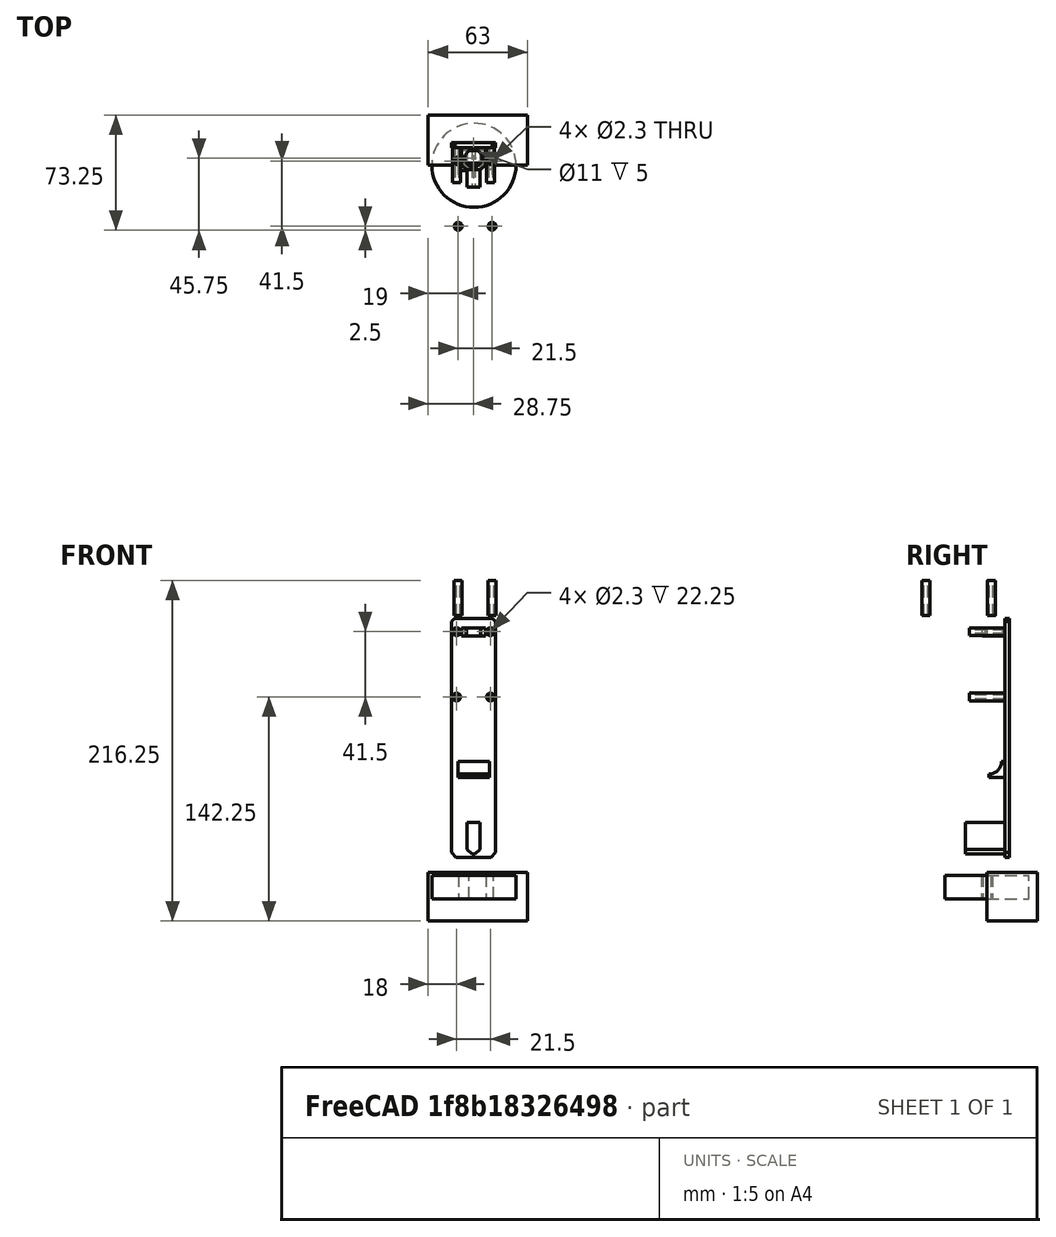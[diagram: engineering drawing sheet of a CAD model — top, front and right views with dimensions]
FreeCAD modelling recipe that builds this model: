
FCSTD DOCUMENT  (FreeCAD 0.19R14555 (Git shallow))
Label: hydrostatus-assembly
License: All rights reserved
LicenseURL: http://en.wikipedia.org/wiki/All_rights_reserved
objects: TechDraw::DrawViewDimension×17, Part::Chamfer×9, Part::Box×6, Part::FeaturePython×6, Part::Cut×3, TechDraw::DrawViewPart×3, Part::Cylinder×2, Sketcher::SketchObject×2, App::LinkGroup×1, PartDesign::ShapeBinder×1, PartDesign::Pad×1, PartDesign::Pocket×1, PartDesign::Body×1, TechDraw::DrawSVGTemplate×1, TechDraw::DrawPage×1
note: 34 computed .brp shape members not serialized (recipe doc carries the construction recipe); baked Part::Feature solids carry a one-line shape summary decoded from their .brp

FEATURE [Part::Box] Box  label="Cube"
  AttacherType = Attacher::AttachEngine3D
  Height = 3
  Length = 28
  Placement = pos=(-13.25,-148.75,-3.25) rot=(0,0,1;0rad)
  Width = 160
FEATURE [Part::Box] Box001  label="Cube001"
  AttacherType = Attacher::AttachEngine3D
  Height = 25
  Length = 8
  Placement = pos=(-3.25,-138.5,0) rot=(0,0,1;0rad)
  Width = 20
FEATURE [Part::Box] Box002  label="Cube002"
  AttacherType = Attacher::AttachEngine3D
  Height = 10
  Length = 20
  Placement = pos=(-9.25,-89.75,-0.25) rot=(0,0,1;0rad)
  Width = 10
FEATURE [Part::Chamfer] Chamfer
  Base = -> Box002
  Edges = 1 edges r=4: [Edge12]
FEATURE [Part::Chamfer] Chamfer001
  Base = -> Box001
  Edges = 1 edges r=3: [Edge5]
FEATURE [Part::Chamfer] Chamfer002
  Base = -> Chamfer001
  Edges = 1 edges r=3: [Edge15]
  Placement = pos=(0,0,-0.25) rot=(0,0,1;0rad)
FEATURE [Part::Cylinder] Cylinder
  Angle = 360
  AttacherType = Attacher::AttachEngine3D
  Height = 64
  Placement = pos=(1,-52.75,6.5) rot=(-1,0,0;1.5708rad)
  Radius = 5.5
FEATURE [Part::Chamfer] Chamfer003
  Base = -> Box
  Edges = 1 edges r=2: [Edge7]
FEATURE [Part::Chamfer] Chamfer004
  Base = -> Chamfer003
  Edges = 1 edges r=2: [Edge15]
FEATURE [Part::Chamfer] Chamfer005
  Base = -> Chamfer004
  Edges = 1 edges r=2: [Edge16]
FEATURE [Part::Chamfer] Chamfer006
  Base = -> Chamfer005
  Edges = 1 edges r=2: [Edge9]
FEATURE [Part::Box] Box003  label="Cube003"
  AttacherType = Attacher::AttachEngine3D
  Height = 14
  Length = 15
  Placement = pos=(-6.5,0,-0.25) rot=(0,0,1;0rad)
  Width = 5
FEATURE [Part::Cut] Cut
  Base = -> Box003
  Tool = -> Cylinder
FEATURE [Part::Chamfer] Chamfer007
  Base = -> Cut
  Edges = 2 edges r=3: [Edge2,Edge10]
  Placement = pos=(-0.25,0,0) rot=(0,0,1;0rad)
FEATURE [Part::FeaturePython] Tube  # WARN: FeaturePython — macro-defined, semantics opaque (R4)
  AttacherType = Attacher::AttachEngine3D
  Height = 22.25
  InnerRadius = 1.15
  OuterRadius = 2.5
  Placement = pos=(-10,-38.75,0) rot=(0,0,1;0rad)
FEATURE [Part::FeaturePython] Tube001  # WARN: FeaturePython — macro-defined, semantics opaque (R4)
  AttacherType = Attacher::AttachEngine3D
  Height = 22.25
  InnerRadius = 1.15
  OuterRadius = 2.5
  Placement = pos=(11.5,-38.75,0) rot=(0,0,1;0rad)
FEATURE [Part::FeaturePython] Tube002  # WARN: FeaturePython — macro-defined, semantics opaque (R4)
  AttacherType = Attacher::AttachEngine3D
  Height = 22.25
  InnerRadius = 1.15
  OuterRadius = 2.5
  Placement = pos=(-10,2.75,0) rot=(0,0,1;0rad)
FEATURE [Part::FeaturePython] Tube003  # WARN: FeaturePython — macro-defined, semantics opaque (R4)
  AttacherType = Attacher::AttachEngine3D
  Height = 22.25
  InnerRadius = 1.15
  OuterRadius = 2.5
  Placement = pos=(11.5,2.75,0) rot=(0,0,1;0rad)
FEATURE [App::LinkGroup] LinkGroup
  ElementList = -> [Tube,Tube001,Tube002,Tube003]
  LinkMode = 0
  Placement = pos=(0,2.38419e-06,-0.250001) rot=(0,0,1;0rad)
FEATURE [Part::Box] Box004  label="Cube004"
  AttacherType = Attacher::AttachEngine3D
  Height = 20
  Length = 38
  Placement = pos=(-18.5,-152.5,-9.75) rot=(0,0,1;0rad)
  Width = 12
FEATURE [Part::Cut] Cut001
  Base = -> Chamfer006
  Tool = -> Box004
FEATURE [Part::Chamfer] Chamfer008
  Base = -> Cut001
  Edges = 2 edges r=3: [Edge9,Edge17]
FEATURE [Part::Cylinder] Cylinder001
  Angle = 360
  AttacherType = Attacher::AttachEngine3D
  Height = 24
  Placement = pos=(12.5,-79.75,9.75) rot=(0,-1,0;1.5708rad)
  Radius = 8
FEATURE [Part::Cut] Cut002
  Base = -> Chamfer
  Tool = -> Cylinder001
FEATURE [Part::FeaturePython] Connect  # WARN: FeaturePython — macro-defined, semantics opaque (R4)
  Objects = -> [Chamfer002,Chamfer007,LinkGroup,Chamfer008,Cut002]
  Placement = pos=(-1,11,-13) rot=(1,0,0;1.5708rad)
  Tolerance = 0
FEATURE [PartDesign::ShapeBinder] CopyPad001
  TraceSupport = false
FEATURE [Sketcher::SketchObject] Sketch002
  FullyConstrained = true
  MapMode = 5
  Placement = pos=(0,0,0) rot=(1,0,0;3.14159rad)
  Support = -> [CopyPad001]
  sketch-geometry (1):
    g0: Circle CenterX=0 CenterY=0 CenterZ=0 NormalX=0 NormalY=0 NormalZ=1 AngleXU=0 Radius=26.72
  constraints (2):
    c: Coincident(g0,g-1)
    c: Diameter(g0) = 53.44
FEATURE [PartDesign::Pad] Pad002
  Direction = (1,1,1)
  Length = 15
  Length2 = 100
  Profile = -> Sketch002
  Type = 0
FEATURE [Sketcher::SketchObject] Sketch003
  FullyConstrained = true
  MapMode = 5
  Placement = pos=(0,0,-15) rot=(1,0,0;3.14159rad)
  Support = -> [Pad002]
  sketch-geometry (2):
    g0: Circle CenterX=-6.45052 CenterY=0 CenterZ=0 NormalX=0 NormalY=0 NormalZ=1 AngleXU=0 Radius=3.475
    g1: Circle CenterX=10.0263 CenterY=0 CenterZ=0 NormalX=0 NormalY=0 NormalZ=1 AngleXU=0 Radius=2.425
  constraints (6):
    c: PointOnObject(g0,g-1)
    c: PointOnObject(g1,g-1)
    c: Diameter(g1) = 4.85
    c: Diameter(g0) = 6.95
    c: DistanceX(g0) = -6.45052
    c: DistanceX(g1) = 10.0263
FEATURE [PartDesign::Pocket] Pocket
  BaseFeature = -> Pad002
  Length = 0
  Length2 = 100
  Profile = -> Sketch003
  Type = 2
FEATURE [PartDesign::Body] Body002  label="pvc_cable_boot"
  Group = -> [CopyPad001,Sketch002,Pad002,Sketch003,Pocket]
  Origin = -> Origin002
  Placement = pos=(0,0,-165) rot=(0,0,1;0rad)
  Tip = -> Pocket
FEATURE [Part::Box] Box005  label="Cube005"
  AttacherType = Attacher::AttachEngine3D
  Height = 31
  Length = 63
  Placement = pos=(-29,0,-194) rot=(0,0,1;0rad)
  Width = 32
FEATURE [Part::FeaturePython] Slice  # WARN: FeaturePython — macro-defined, semantics opaque (R4)
  Base = -> Body002
  Mode = 1
  Tolerance = 0
  Tools = -> [Box005]
FEATURE [TechDraw::DrawSVGTemplate] Template
  Height = 210
  Orientation = 1
  Width = 297
FEATURE [TechDraw::DrawViewPart] View
  Caption = electronics assembly top view
  CoarseView = false
  Direction = (0,-1,0)
  Focus = 100
  HardHidden = false
  IsoCount = 0
  IsoHidden = false
  IsoVisible = false
  LockPosition = false
  Perspective = false
  Rotation = 0
  ScaleType = 0
  SeamHidden = false
  SeamVisible = true
  SmoothHidden = false
  SmoothVisible = true
  Source = -> [Connect]
  X = 149.857
  XDirection = (0,0,-1)
  Y = 53.4468
FEATURE [TechDraw::DrawViewPart] View001
  Caption = electronics assembly 45*d view
  CoarseView = false
  Direction = (-0.707,-0.707,0)
  Focus = 100
  HardHidden = false
  IsoCount = 0
  IsoHidden = false
  IsoVisible = false
  LockPosition = false
  Perspective = false
  Rotation = 0
  ScaleType = 0
  SeamHidden = false
  SeamVisible = true
  SmoothHidden = false
  SmoothVisible = true
  Source = -> [Connect]
  X = 149.857
  XDirection = (0,0,-1)
  Y = 106.017
FEATURE [TechDraw::DrawViewPart] View002
  Caption = electronics assembly side profile
  CoarseView = false
  Direction = (-1,0,0)
  Focus = 100
  HardHidden = false
  IsoCount = 0
  IsoHidden = false
  IsoVisible = false
  LockPosition = false
  Perspective = false
  Rotation = 0
  ScaleType = 0
  SeamHidden = false
  SeamVisible = true
  SmoothHidden = false
  SmoothVisible = true
  Source = -> [Connect]
  X = 149.857
  XDirection = (0,0,-1)
  Y = 158.249
FEATURE [TechDraw::DrawViewDimension] Dimension
  Arbitrary = false
  ArbitraryTolerances = false
  EqualTolerance = true
  FormatSpec = %.2f
  FormatSpecOverTolerance = %+.2f
  FormatSpecUnderTolerance = %+.2f
  Inverted = false
  LockPosition = false
  MeasureType = 1
  OverTolerance = 0
  References2D = -> [View]
  Rotation = 0
  ScaleType = 0
  TheoreticalExact = false
  Type = 2
  UnderTolerance = 0
  X = 79.6211
  Y = -9.54121
FEATURE [TechDraw::DrawViewDimension] Dimension001
  Arbitrary = false
  ArbitraryTolerances = false
  EqualTolerance = true
  FormatSpec = %.2f
  FormatSpecOverTolerance = %+.2f
  FormatSpecUnderTolerance = %+.2f
  Inverted = false
  LockPosition = false
  MeasureType = 1
  OverTolerance = 0
  References2D = -> [View]
  Rotation = 0
  ScaleType = 0
  TheoreticalExact = false
  Type = 1
  UnderTolerance = 0
  X = 39.1592
  Y = 23.0334
FEATURE [TechDraw::DrawViewDimension] Dimension002
  Arbitrary = false
  ArbitraryTolerances = false
  EqualTolerance = true
  FormatSpec = %.2f
  FormatSpecOverTolerance = %+.2f
  FormatSpecUnderTolerance = %+.2f
  Inverted = false
  LockPosition = false
  MeasureType = 1
  OverTolerance = 0
  References2D = -> [View]
  Rotation = 0
  ScaleType = 0
  TheoreticalExact = false
  Type = 2
  UnderTolerance = 0
  X = 10.3544
  Y = 0.227172
FEATURE [TechDraw::DrawViewDimension] Dimension003
  Arbitrary = false
  ArbitraryTolerances = false
  EqualTolerance = true
  FormatSpec = %.2f
  FormatSpecOverTolerance = %+.2f
  FormatSpecUnderTolerance = %+.2f
  Inverted = false
  LockPosition = false
  MeasureType = 1
  OverTolerance = 0
  References2D = -> [View]
  Rotation = 0
  ScaleType = 0
  TheoreticalExact = false
  Type = 1
  UnderTolerance = 0
  X = 62.375
  Y = -6.83965
FEATURE [TechDraw::DrawViewDimension] Dimension005
  Arbitrary = false
  ArbitraryTolerances = false
  EqualTolerance = true
  FormatSpec = %.2f
  FormatSpecOverTolerance = %+.2f
  FormatSpecUnderTolerance = %+.2f
  Inverted = false
  LockPosition = false
  MeasureType = 1
  OverTolerance = 0
  References2D = -> [View002]
  Rotation = 0
  ScaleType = 0
  TheoreticalExact = false
  Type = 2
  UnderTolerance = 0
  X = 78.7503
  Y = 3.43096
FEATURE [TechDraw::DrawViewDimension] Dimension006
  Arbitrary = false
  ArbitraryTolerances = false
  EqualTolerance = true
  FormatSpec = ⌀%.2f
  FormatSpecOverTolerance = %+.2f
  FormatSpecUnderTolerance = %+.2f
  Inverted = false
  LockPosition = false
  MeasureType = 1
  OverTolerance = 0
  References2D = -> [View]
  Rotation = 0
  ScaleType = 0
  TheoreticalExact = false
  Type = 5
  UnderTolerance = 0
  X = -15.8415
  Y = -7.03338
FEATURE [TechDraw::DrawViewDimension] Dimension007
  Arbitrary = false
  ArbitraryTolerances = false
  EqualTolerance = true
  FormatSpec = ⌀%.2f
  FormatSpecOverTolerance = %+.2f
  FormatSpecUnderTolerance = %+.2f
  Inverted = false
  LockPosition = false
  MeasureType = 1
  OverTolerance = 0
  References2D = -> [View]
  Rotation = 0
  ScaleType = 0
  TheoreticalExact = false
  Type = 5
  UnderTolerance = 0
  X = -19.4568
  Y = -0.52586
FEATURE [TechDraw::DrawViewDimension] Dimension008
  Arbitrary = false
  ArbitraryTolerances = false
  EqualTolerance = true
  FormatSpec = %.2f
  FormatSpecOverTolerance = %+.2f
  FormatSpecUnderTolerance = %+.2f
  Inverted = false
  LockPosition = false
  MeasureType = 1
  OverTolerance = 0
  References2D = -> [View]
  Rotation = 0
  ScaleType = 0
  TheoreticalExact = false
  Type = 2
  UnderTolerance = 0
  X = -60.2209
  Y = 1.31465
FEATURE [TechDraw::DrawViewDimension] Dimension009
  Arbitrary = false
  ArbitraryTolerances = false
  EqualTolerance = true
  FormatSpec = %.2f
  FormatSpecOverTolerance = %+.2f
  FormatSpecUnderTolerance = %+.2f
  Inverted = false
  LockPosition = false
  MeasureType = 1
  OverTolerance = 0
  References2D = -> [View]
  Rotation = 0
  ScaleType = 0
  TheoreticalExact = false
  Type = 2
  UnderTolerance = 0
  X = -73.6196
  Y = 0.920256
FEATURE [TechDraw::DrawViewDimension] Dimension010
  Arbitrary = false
  ArbitraryTolerances = false
  EqualTolerance = true
  FormatSpec = %.2f
  FormatSpecOverTolerance = %+.2f
  FormatSpecUnderTolerance = %+.2f
  Inverted = false
  LockPosition = false
  MeasureType = 1
  OverTolerance = 0
  References2D = -> [View]
  Rotation = 0
  ScaleType = 0
  TheoreticalExact = false
  Type = 1
  UnderTolerance = 0
  X = -46.9537
  Y = 20.8728
FEATURE [TechDraw::DrawViewDimension] Dimension011
  Arbitrary = false
  ArbitraryTolerances = false
  EqualTolerance = true
  FormatSpec = %.2f
  FormatSpecOverTolerance = %+.2f
  FormatSpecUnderTolerance = %+.2f
  Inverted = false
  LockPosition = false
  MeasureType = 1
  OverTolerance = 0
  References2D = -> [View]
  Rotation = 0
  ScaleType = 0
  TheoreticalExact = false
  Type = 2
  UnderTolerance = 0
  X = -84.1007
  Y = -0.113585
FEATURE [TechDraw::DrawViewDimension] Dimension012
  Arbitrary = false
  ArbitraryTolerances = false
  EqualTolerance = true
  FormatSpec = %.2f
  FormatSpecOverTolerance = %+.2f
  FormatSpecUnderTolerance = %+.2f
  Inverted = false
  LockPosition = false
  MeasureType = 1
  OverTolerance = 0
  References2D = -> [View002]
  Rotation = 0
  ScaleType = 0
  TheoreticalExact = false
  Type = 2
  UnderTolerance = 0
  X = -80.6456
  Y = -12.3864
FEATURE [TechDraw::DrawViewDimension] Dimension013
  Arbitrary = false
  ArbitraryTolerances = false
  EqualTolerance = true
  FormatSpec = %.2f
  FormatSpecOverTolerance = %+.2f
  FormatSpecUnderTolerance = %+.2f
  Inverted = false
  LockPosition = false
  MeasureType = 1
  OverTolerance = 0
  References2D = -> [View002]
  Rotation = 0
  ScaleType = 0
  TheoreticalExact = false
  Type = 2
  UnderTolerance = 0
  X = -74.532
  Y = 1.48803
FEATURE [TechDraw::DrawViewDimension] Dimension014
  Arbitrary = false
  ArbitraryTolerances = false
  EqualTolerance = true
  FormatSpec = %.2f
  FormatSpecOverTolerance = %+.2f
  FormatSpecUnderTolerance = %+.2f
  Inverted = false
  LockPosition = false
  MeasureType = 1
  OverTolerance = 0
  References2D = -> [View002]
  Rotation = 0
  ScaleType = 0
  TheoreticalExact = false
  Type = 1
  UnderTolerance = 0
  X = -46.3978
  Y = 18.0652
FEATURE [TechDraw::DrawViewDimension] Dimension015
  Arbitrary = false
  ArbitraryTolerances = false
  EqualTolerance = true
  FormatSpec = %.2f
  FormatSpecOverTolerance = %+.2f
  FormatSpecUnderTolerance = %+.2f
  Inverted = false
  LockPosition = false
  MeasureType = 1
  OverTolerance = 0
  References2D = -> [View002]
  Rotation = 0
  ScaleType = 0
  TheoreticalExact = false
  Type = 1
  UnderTolerance = 0
  X = 62.1478
  Y = 20.4744
FEATURE [TechDraw::DrawViewDimension] Dimension016
  Arbitrary = false
  ArbitraryTolerances = false
  EqualTolerance = true
  FormatSpec = %.2f
  FormatSpecOverTolerance = %+.2f
  FormatSpecUnderTolerance = %+.2f
  Inverted = false
  LockPosition = false
  MeasureType = 1
  OverTolerance = 0
  References2D = -> [View002]
  Rotation = 0
  ScaleType = 0
  TheoreticalExact = false
  Type = 2
  UnderTolerance = 0
  X = 22.4107
  Y = 6.17619
FEATURE [TechDraw::DrawViewDimension] Dimension017
  Arbitrary = false
  ArbitraryTolerances = false
  EqualTolerance = true
  FormatSpec = %.2f
  FormatSpecOverTolerance = %+.2f
  FormatSpecUnderTolerance = %+.2f
  Inverted = false
  LockPosition = false
  MeasureType = 1
  OverTolerance = 0
  References2D = -> [View002]
  Rotation = 0
  ScaleType = 0
  TheoreticalExact = false
  Type = 1
  UnderTolerance = 0
  X = 39.02
  Y = -2.77927
FEATURE [TechDraw::DrawPage] Page
  KeepUpdated = true
  NextBalloonIndex = 1
  ProjectionType = 0
  Template = -> Template
  Views = -> [View,View001,View002,Dimension,Dimension001,Dimension002,Dimension003,Dimension005,Dimension006,Dimension007,Dimension008,Dimension009,Dimension010,Dimension011,Dimension012,Dimension013,Dimension014,Dimension015,Dimension016,Dimension017]
